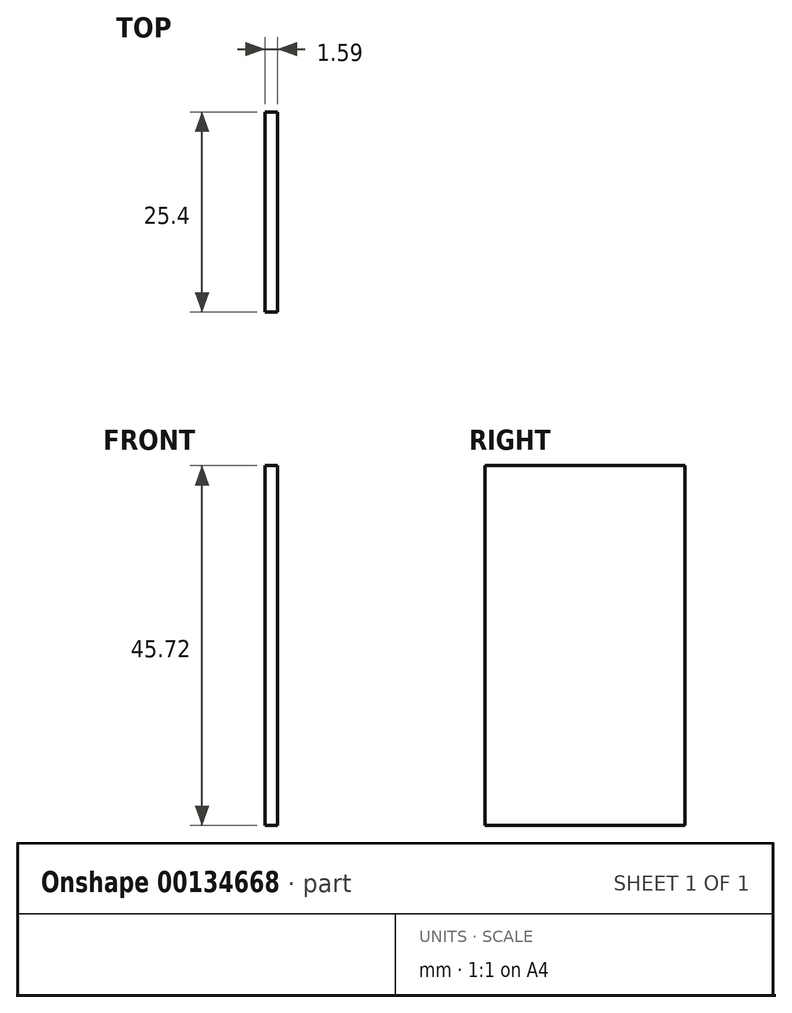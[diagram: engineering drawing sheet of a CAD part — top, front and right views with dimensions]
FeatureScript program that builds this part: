
annotation { "Feature Type Name" : "Feature", "Feature Type Description" : "" }
export const myFeature = defineFeature(function(context is Context, id is Id, definition is map)
    precondition{}
    {
        {
            var Q0;
            Q0=qCreatedBy(makeId("Right.planeOp"),FACE);
            var sketch = newSketch(context, id + "F0", { "sketchPlane" : qUnion([Q0])});
            skLineSegment(sketch, "E0.bottom", {"start": v(12.7, -22.86) * mm, "end": v(-12.7, -22.86) * mm});
            skLineSegment(sketch, "E0.top", {"start": v(12.7, 22.86) * mm, "end": v(-12.7, 22.86) * mm});
            skLineSegment(sketch, "E0.left", {"start": v(12.7, -22.86) * mm, "end": v(12.7, 22.86) * mm});
            skLineSegment(sketch, "E0.right", {"start": v(-12.7, -22.86) * mm, "end": v(-12.7, 22.86) * mm});
            skPoint(sketch, "E0.middle", {"position": v(0, 0) * mm});
            skSolve(sketch);
        }
        {
            var Q0;
            Q0 = qSketchRegion(id + "F0", true);
            extrude(context, id + "F1", {"entities" : qUnion([Q0]), "depth" : 1.59 * mm});
        }
    });
